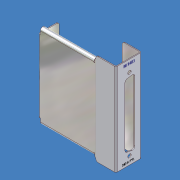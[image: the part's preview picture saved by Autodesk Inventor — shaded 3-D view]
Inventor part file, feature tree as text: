
AUTODESK INVENTOR PART (.ipt)
format: ipt  version: unknown  size: 564,224 bytes
history: native  units: mm (DEFAULTED — no unit token found)
features: sheet_metal_op x11, sketch x11, other x9, chamfer x3
ambient origin geometry x8: Origin, YZ Plane, XZ Plane, XY Plane, X Axis, Y Axis, Z Axis, Center Point
feature tree (34):
  sheet_metal_op  "Face1"
  sheet_metal_op  "Flange1"
  sheet_metal_op  "Flange2"
  chamfer  "Corner Round1"
  sheet_metal_op  "Face2"
  sheet_metal_op  "Flange3"
  chamfer  "Corner Round2"
  sheet_metal_op  "Hem2"
  sheet_metal_op  "Hem3"
  chamfer  "Corner Round3"
  sketch  "Sketch1"  dims[d0=22.86mm]
  other  "Plate1"
  sketch  "Sketch2"  dims[d1=80.5688mm]
  other  "Plate2"
  sheet_metal_op  "Bend1"
  sketch  "Sketch3"  dims[d2=0.7874mm]
  other  "Plate3"
  sheet_metal_op  "Bend2"
  sketch  "Sketch4"  dims[d3=0.7874mm]
  other  "Plate4"
  sheet_metal_op  "Bend3"
  sketch  "Sketch5"  dims[d4=0.3937mm]
  other  "Plate5"
  sheet_metal_op  "Bend4"
  sketch  "Sketch8"  dims[d5=1.5748mm]
  sketch  "Sketch9"  dims[d6=0.7874mm]
  sketch  "Sketch10"  dims[d7=16.51mm d8=90.0deg d9=0.7874mm]
  sketch  "Sketch11"  dims[d10=0.7874mm]
  sketch  "Sketch12"  dims[d11=0.3937mm]
  sketch  "Sketch15"  dims[d12=1.5748mm d13=0.7874mm d14=17.526mm d15=90.0deg d16=0.7874mm d17=1.778mm d18=0.7874mm d19=0.7874mm d20=0.3937mm d21=1.5748mm d22=0.7874mm d23=73.66mm d24=50.8mm d25=5.08mm d26=5.08mm d27=0.7874mm d28=0.3937mm d29=1.5748mm d30=0.7874mm d31=17.78mm d32=90.0deg d33=0.7874mm d42=1.778mm d43=0.7874mm d44=0.0mm d45=0.7874mm d46=0.3937mm d47=1.5748mm d48=0.7874mm d49=3.1496mm d50=2.7432mm d51=1.3716mm d52=0.7874mm d53=0.3937mm d54=1.5748mm d55=0.7874mm d56=3.1496mm d57=2.7432mm d58=1.3716mm d59=12.7mm d60=20.32mm d62=5.588mm d63=0.7874mm d64=0.0mm d65=1.778mm d66=3.175mm d67=3.048mm d69=31.75mm d76=38.7604mm d78=0.508mm d99=-15.707963mm]
  other  "Image5"
  other  "Cut1"
  other  "Cut2"
  other  "iFeature14:1"
